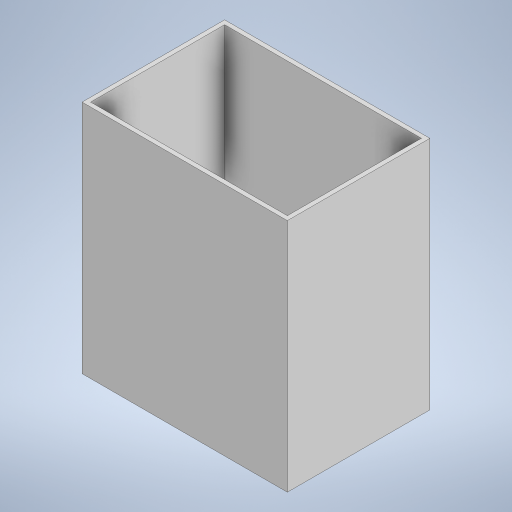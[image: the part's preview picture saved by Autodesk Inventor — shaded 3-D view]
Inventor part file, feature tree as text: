
AUTODESK INVENTOR PART (.ipt)
format: ipt  version: 2024 (Build 280153000, 153)  size: 196,608 bytes
history: native  units: mm
features: extrude x2, sketch x2
ambient origin geometry x8: Origin, YZ Plane, XZ Plane, XY Plane, X Axis, Y Axis, Z Axis, Center Point
bodies: Body1 (feature_tree)
feature tree (4):
  extrude  "Extrusión2"  Depth=50.0mm
  extrude  "Extrusión3"  Depth=1.5mm
  sketch  "Boceto3"  dims[d8=72.0mm d9=50.0mm]
  sketch  "Boceto5"  dims[d10=82.5mm d11=0.0mm d12=1.5mm d13=1.5mm d14=1.5mm d15=1.5mm d16=81.0mm d17=0.0mm]
